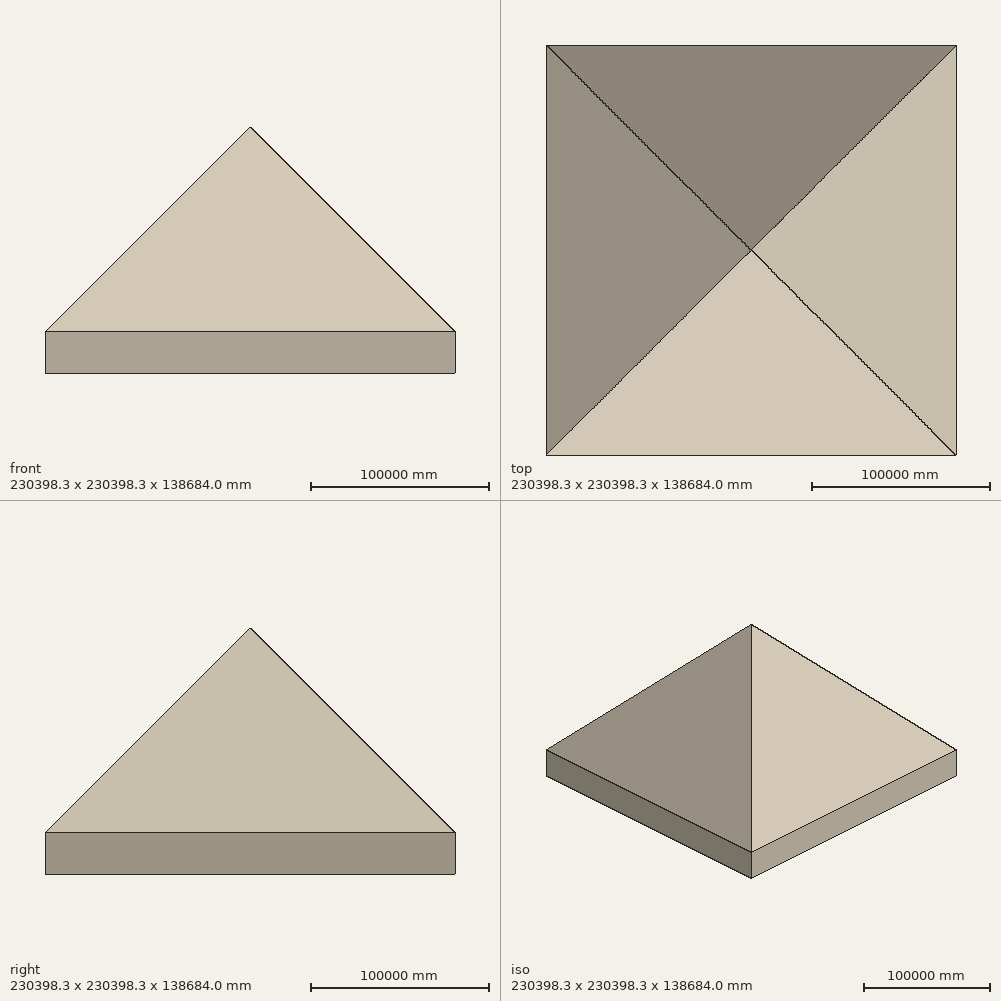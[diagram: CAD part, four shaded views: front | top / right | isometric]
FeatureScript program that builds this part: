
annotation { "Feature Type Name" : "Feature", "Feature Type Description" : "" }
export const myFeature = defineFeature(function(context is Context, id is Id, definition is map)
    precondition{}
    {
        {
            var Q0;
            Q0=qCreatedBy(makeId("Top.planeOp"),FACE);
            var sketch = newSketch(context, id + "F0", { "sketchPlane" : qUnion([Q0])});
            skLineSegment(sketch, "E0", {"start": v(0, 0) * mm, "end": v(230398.32, 0) * mm});
            skLineSegment(sketch, "E1", {"start": v(0, 0) * mm, "end": v(0, 230398.32) * mm});
            skLineSegment(sketch, "E2", {"start": v(0, 230398.32) * mm, "end": v(230398.32, 230398.32) * mm});
            skLineSegment(sketch, "E3", {"start": v(230398.32, 230398.32) * mm, "end": v(230398.32, 0) * mm});
            skSolve(sketch);
        }
        {
            var Q0;
            Q0=makeQuery(id+"F0.imprint","IMPRINT",FACE,{"disambiguationData":[TD([[makeQuery(id+"F0.imprint","IMPRINT",EDGE,{"derivedFrom":sQuery(id+"F0.wireOp",EDGE,"E0")}),1.0]])]});
            extrude(context, id + "F1", {"entities" : qUnion([Q0]), "depth" : 138684 * mm, "offsetDistance" : 30.48 * mm});
        }
        {
            var Q0;
            Q0=makeQuery(id+"F1.opExtrude","CAP_EDGE",EDGE,{"disambiguationData":[OSD([sQuery(id+"F0.wireOp",EDGE,"E1")])],"isStart":false});
            var Q1;
            Q1=makeQuery(id+"F1.opExtrude","CAP_EDGE",EDGE,{"disambiguationData":[OSD([sQuery(id+"F0.wireOp",EDGE,"E2")])],"isStart":false});
            var Q2;
            Q2=makeQuery(id+"F1.opExtrude","CAP_EDGE",EDGE,{"disambiguationData":[OSD([sQuery(id+"F0.wireOp",EDGE,"E3")])],"isStart":false});
            var Q3;
            Q3=makeQuery(id+"F1.opExtrude","CAP_EDGE",EDGE,{"disambiguationData":[OSD([sQuery(id+"F0.wireOp",EDGE,"E0")])],"isStart":false});
            chamfer(context, id + "F2", {"entities" : qUnion([Q0, Q1, Q2, Q3]), "width" : 114909.6 * mm, "tangentPropagation" : true});
        }
    });
